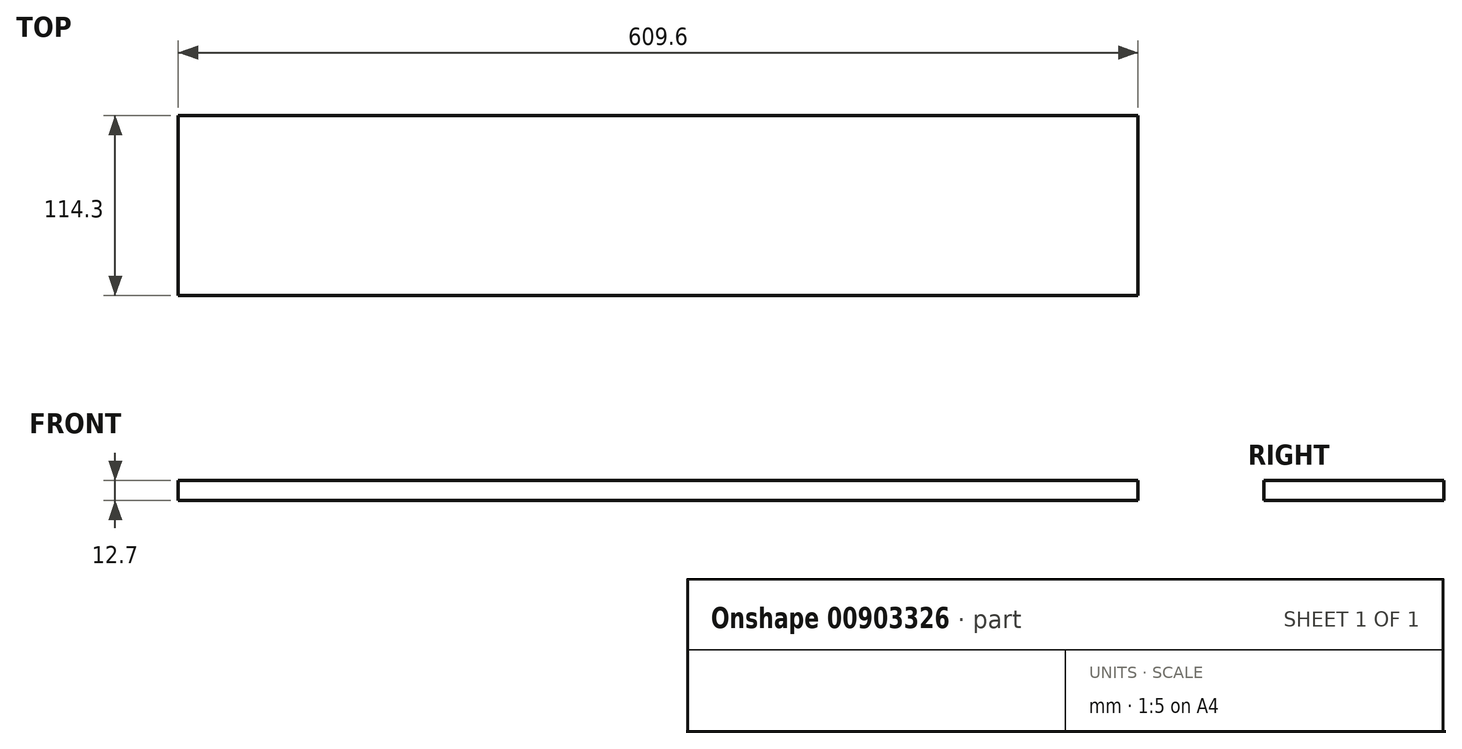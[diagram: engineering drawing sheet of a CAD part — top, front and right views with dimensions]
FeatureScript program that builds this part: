
annotation { "Feature Type Name" : "Feature", "Feature Type Description" : "" }
export const myFeature = defineFeature(function(context is Context, id is Id, definition is map)
    precondition{}
    {
        {
            var Q0;
            Q0=qCreatedBy(makeId("Right.planeOp"),FACE);
            var sketch = newSketch(context, id + "F0", { "sketchPlane" : qUnion([Q0])});
            skLineSegment(sketch, "E0.bottom", {"start": v(-56.49, 6.28) * mm, "end": v(57.81, 6.28) * mm});
            skLineSegment(sketch, "E0.top", {"start": v(-56.49, -6.42) * mm, "end": v(57.81, -6.42) * mm});
            skLineSegment(sketch, "E0.left", {"start": v(-56.49, 6.28) * mm, "end": v(-56.49, -6.42) * mm});
            skLineSegment(sketch, "E0.right", {"start": v(57.81, 6.28) * mm, "end": v(57.81, -6.42) * mm});
            skSolve(sketch);
        }
        {
            var Q0;
            Q0=makeQuery(id+"F0.imprint","IMPRINT",FACE,{"disambiguationData":[TD([[makeQuery(id+"F0.imprint","IMPRINT",EDGE,{"derivedFrom":sQuery(id+"F0.wireOp",EDGE,"E0.bottom")}),-1.0]])]});
            extrude(context, id + "F1", {"entities" : qUnion([Q0]), "depth" : 609.6 * mm, "offsetDistance" : 25.4 * mm});
        }
    });
